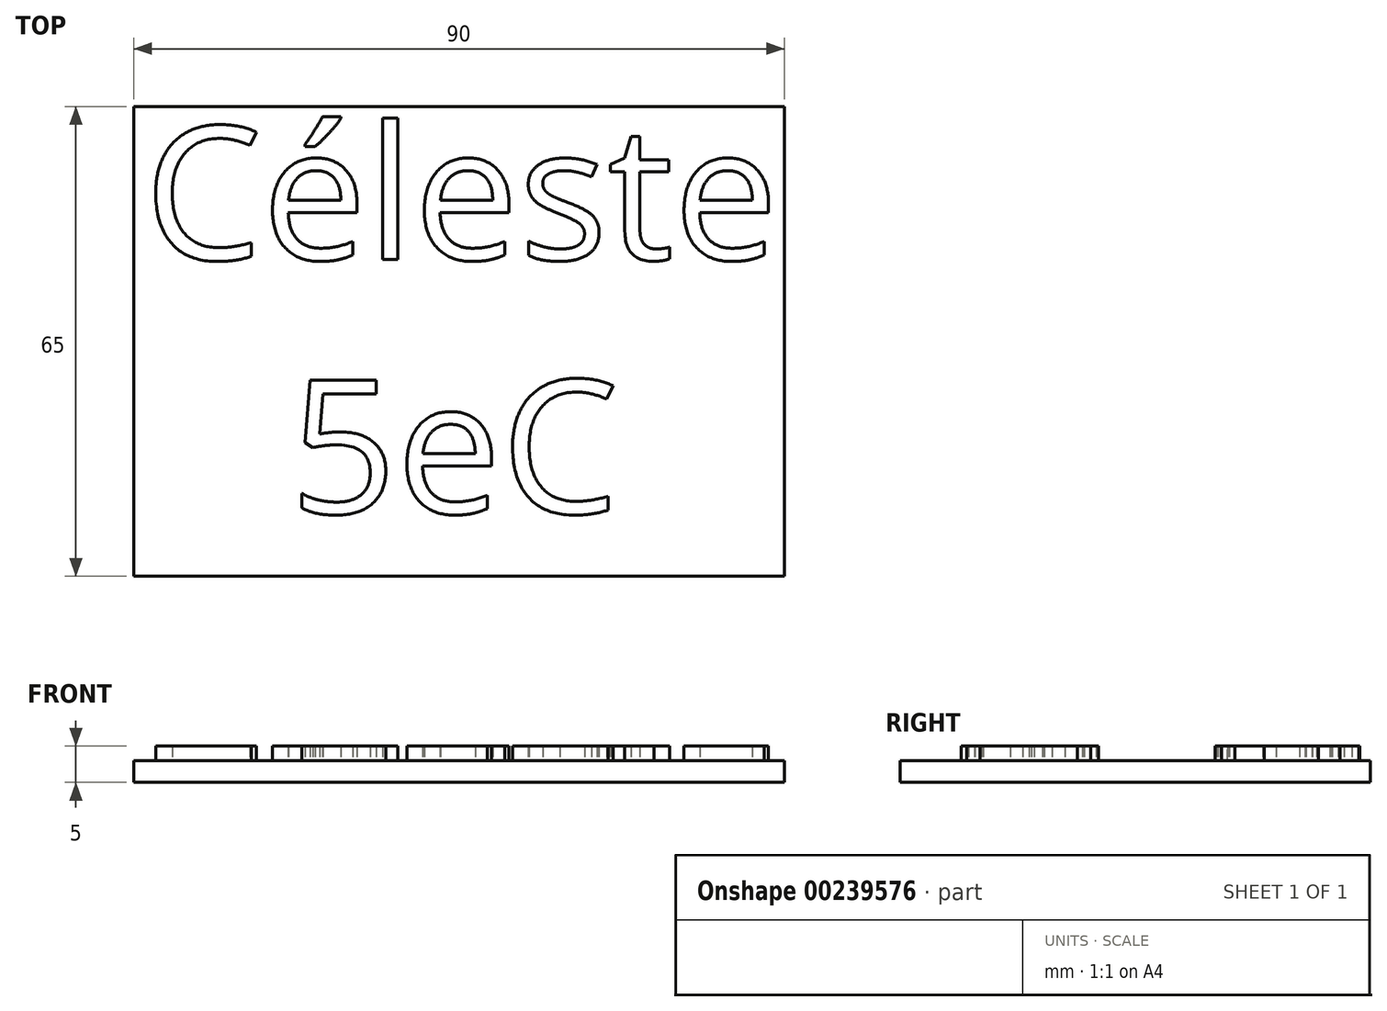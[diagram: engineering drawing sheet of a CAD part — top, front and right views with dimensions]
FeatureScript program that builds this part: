
annotation { "Feature Type Name" : "Feature", "Feature Type Description" : "" }
export const myFeature = defineFeature(function(context is Context, id is Id, definition is map)
    precondition{}
    {
        {
            var Q0;
            Q0=qCreatedBy(makeId("Top.planeOp"),FACE);
            var sketch = newSketch(context, id + "F0", { "sketchPlane" : qUnion([Q0])});
            skLineSegment(sketch, "E0.bottom", {"start": v(0, 0) * mm, "end": v(90, 0) * mm});
            skLineSegment(sketch, "E0.top", {"start": v(0, -65) * mm, "end": v(90, -65) * mm});
            skLineSegment(sketch, "E0.left", {"start": v(0, 0) * mm, "end": v(0, -65) * mm});
            skLineSegment(sketch, "E0.right", {"start": v(90, 0) * mm, "end": v(90, -65) * mm});
            skSolve(sketch);
        }
        {
            var Q0;
            Q0=makeQuery(id+"F0.imprint","IMPRINT",FACE,{"disambiguationData":[TD([[makeQuery(id+"F0.imprint","IMPRINT",EDGE,{"derivedFrom":sQuery(id+"F0.wireOp",EDGE,"E0.bottom")}),-1.0]])]});
            extrude(context, id + "F1", {"entities" : qUnion([Q0]), "depth" : 3 * mm});
        }
        {
            var Q0;
            Q0=makeQuery(id+"F1.opExtrude","CAP_FACE",FACE,{"disambiguationData":[OSD([sQuery(id+"F0.wireOp",EDGE,"E0.bottom"),sQuery(id+"F0.wireOp",EDGE,"E0.top"),sQuery(id+"F0.wireOp",EDGE,"E0.left"),sQuery(id+"F0.wireOp",EDGE,"E0.right")])],"isStart":false});
            var sketch = newSketch(context, id + "F2", { "sketchPlane" : qUnion([Q0])});
            skText(sketch, "E1", { "text": "Céleste\n   5eC", "fontName": "OpenSans-Regular.ttf"});
            const initialGuessF2  = {"E1": [0.00148, -0.02119, 1, 0, 0.01858]};
            skSetInitialGuess(sketch, initialGuessF2);
            skSolve(sketch);
        }
        {
            var Q0;
            Q0 = qSketchRegion(id + "F2", true);
            extrude(context, id + "F3", {"entities" : qUnion([Q0]), "operationType" : NewBodyOperationType.ADD, "depth" : 2 * mm});
        }
    });
